# Revit family: Пульт управления центральный ВклВыкл  ESVM-J01C
name_source: partatom
category: Mechanical Equipment
revit_build: Autodesk Revit 2016 (Build: 20150506_1715(x64)
units: mm (PartAtom-declared; Revit-internal decimal feet)

## family parameters
Cut with Voids When Loaded = No
Host = Face
Part Type = Normal
Room Calculation Point = No
Round Connector Dimension = Use Diameter
Shared = No

## types (1)
- ESVM-J01C
    Default Elevation = 1219.2 mm  [stored 4 ft]
    Артикул = 1090049
    Вес = 0.30 kg
    Высота = 120 mm  [stored 0.393701 ft]
    Глубина = 20 mm  [stored 0.0656168 ft]
    Максимальное кол-во подключаемых внутренних блоков, шт = 256
    Модель = ESVM-J01C
    Наименование = Пульт управления центральный Вкл/Выкл
    Производитель = Electrolux
    Таблица модель = Модель
    Таблица наименование = Наименование
    Таблица параметров = Таблица параметров
    Таблица частота сети = Частота сети
    Таблица электропитание = Электропитание
    Частота сети (DC) = сигнальный кабель постоянный ток (DC)
    Ширина = 120 mm  [stored 0.393701 ft]
    Эл. питание(коннектор) = 5 V
    Электропитание, (В) = 5

note: [stored X ft] marks values corroborated as IEEE doubles in the binary element streams (Revit-internal decimal feet)
